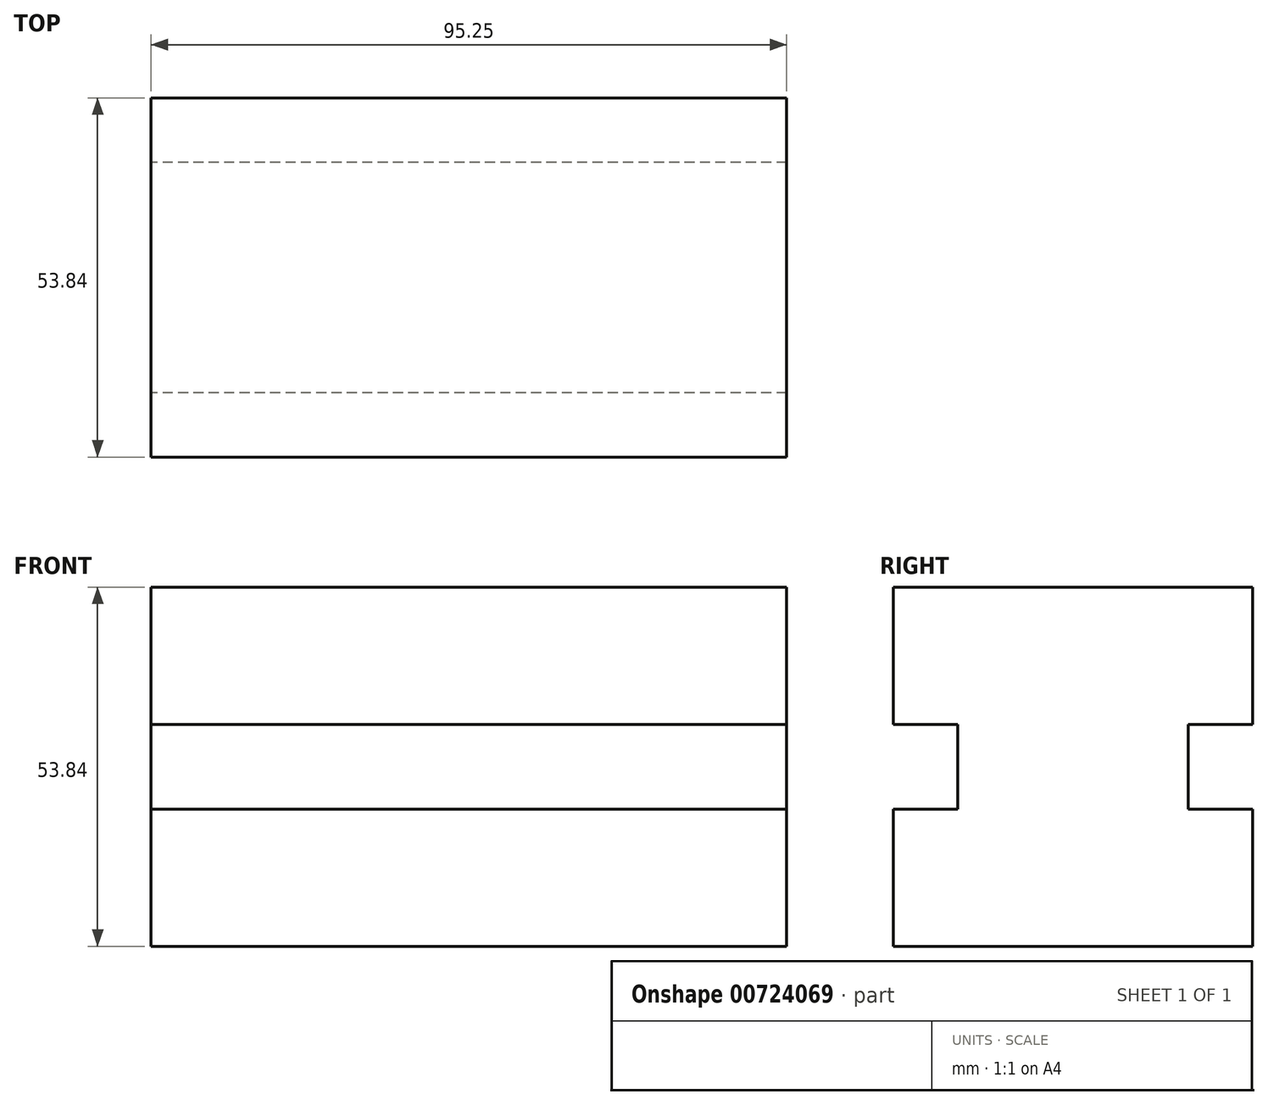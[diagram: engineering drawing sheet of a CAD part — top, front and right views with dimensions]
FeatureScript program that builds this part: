
annotation { "Feature Type Name" : "Feature", "Feature Type Description" : "" }
export const myFeature = defineFeature(function(context is Context, id is Id, definition is map)
    precondition{}
    {
        {
            var Q0;
            Q0=qCreatedBy(makeId("Right.planeOp"),FACE);
            var sketch = newSketch(context, id + "F0", { "sketchPlane" : qUnion([Q0])});
            skLineSegment(sketch, "E0.bottom", {"start": v(26.92, 26.92) * mm, "end": v(-26.92, 26.92) * mm});
            skLineSegment(sketch, "E0.top", {"start": v(26.92, -26.92) * mm, "end": v(-26.92, -26.92) * mm});
            skLineSegment(sketch, "E0.left", {"start": v(26.92, 26.92) * mm, "end": v(26.92, 6.35) * mm});
            skLineSegment(sketch, "E0.right", {"start": v(-26.92, 26.92) * mm, "end": v(-26.92, 6.35) * mm});
            skPoint(sketch, "E0.middle", {"position": v(0, 0) * mm});
            skLineSegment(sketch, "E1.bottom", {"start": v(-26.92, 6.35) * mm, "end": v(-17.27, 6.35) * mm});
            skLineSegment(sketch, "E1.top", {"start": v(-26.92, -6.35) * mm, "end": v(-17.27, -6.35) * mm});
            skLineSegment(sketch, "E1.right", {"start": v(-17.27, 6.35) * mm, "end": v(-17.27, -6.35) * mm});
            skLineSegment(sketch, "E2.trimOffspring", {"start": v(-26.92, -6.35) * mm, "end": v(-26.92, -26.92) * mm});
            skLineSegment(sketch, "E3", {"start": v(0, 30.15) * mm, "end": v(0, -41.23) * mm, "construction": true});
            skLineSegment(sketch, "E4.MirrorCS", {"start": v(26.92, 6.35) * mm, "end": v(17.27, 6.35) * mm});
            skLineSegment(sketch, "E5.MirrorCS", {"start": v(17.27, 6.35) * mm, "end": v(17.27, -6.35) * mm});
            skLineSegment(sketch, "E6.MirrorCS", {"start": v(26.92, -6.35) * mm, "end": v(17.27, -6.35) * mm});
            skLineSegment(sketch, "E7.trimOffspring", {"start": v(26.92, -6.35) * mm, "end": v(26.92, -26.92) * mm});
            skSolve(sketch);
        }
        {
            var Q0;
            Q0 = qSketchRegion(id + "F0", true);
            extrude(context, id + "F1", {"entities" : qUnion([Q0]), "depth" : 95.25 * mm, "offsetDistance" : 25.4 * mm});
        }
    });
